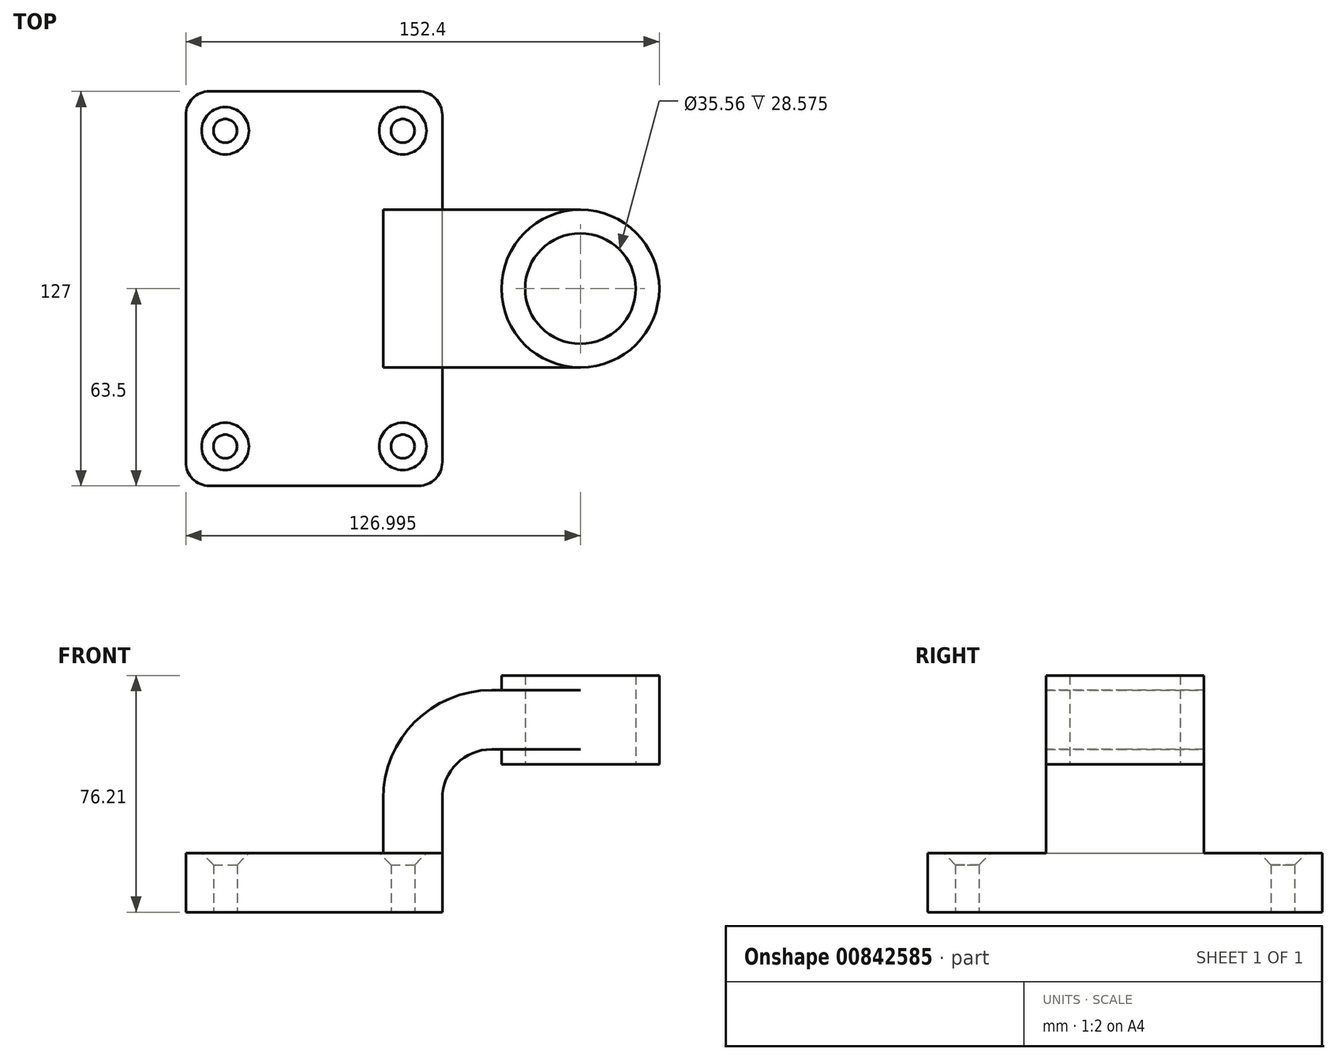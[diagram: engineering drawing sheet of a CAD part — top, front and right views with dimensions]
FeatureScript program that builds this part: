
annotation { "Feature Type Name" : "Feature", "Feature Type Description" : "" }
export const myFeature = defineFeature(function(context is Context, id is Id, definition is map)
    precondition{}
    {
        {
            var Q0;
            Q0=qCreatedBy(makeId("Front.planeOp"),FACE);
            var sketch = newSketch(context, id + "F0", { "sketchPlane" : qUnion([Q0])});
            skLineSegment(sketch, "E0.bottom", {"start": v(-41.28, 9.52) * mm, "end": v(41.27, 9.53) * mm});
            skLineSegment(sketch, "E0.top", {"start": v(-41.28, -9.53) * mm, "end": v(41.28, -9.53) * mm});
            skLineSegment(sketch, "E0.left", {"start": v(-41.28, 9.52) * mm, "end": v(-41.27, -9.53) * mm});
            skLineSegment(sketch, "E0.right", {"start": v(41.28, 9.53) * mm, "end": v(41.28, -9.52) * mm});
            skPoint(sketch, "E0.middle", {"position": v(0, 0) * mm});
            skLineSegment(sketch, "E1.bottom", {"start": v(111.13, 38.1) * mm, "end": v(60.33, 38.1) * mm});
            skLineSegment(sketch, "E1.top", {"start": v(111.13, 66.67) * mm, "end": v(60.33, 66.67) * mm});
            skLineSegment(sketch, "E1.left", {"start": v(111.13, 38.1) * mm, "end": v(111.13, 66.67) * mm});
            skLineSegment(sketch, "E1.right", {"start": v(60.33, 38.1) * mm, "end": v(60.33, 66.67) * mm});
            skPoint(sketch, "E1.middle", {"position": v(85.73, 52.39) * mm});
            skLineSegment(sketch, "E2", {"start": v(41.27, 9.53) * mm, "end": v(41.27, 27) * mm});
            skArc(sketch, "E3", {"start": v(41.27, 27) * mm, "mid": v(45.92, 38.23) * mm, "end": v(57.15, 42.88) * mm});
            skLineSegment(sketch, "E4", {"start": v(57.15, 42.88) * mm, "end": v(85.73, 42.88) * mm});
            skLineSegment(sketch, "E5.0", {"start": v(57.15, 61.93) * mm, "end": v(85.73, 61.93) * mm});
            skArc(sketch, "E5.1", {"start": v(22.22, 27) * mm, "mid": v(32.45, 51.7) * mm, "end": v(57.15, 61.93) * mm});
            skLineSegment(sketch, "E5.2", {"start": v(22.22, 9.53) * mm, "end": v(22.22, 27) * mm});
            skLineSegment(sketch, "E6", {"start": v(85.73, 38.1) * mm, "end": v(85.73, 66.67) * mm});
            skFitSpline(sketch, "E7", {"points": [v(-41.28, 9.53) * mm, v(57.15, 61.93) * mm], "startDerivative": vector(-0.26, 81.95) * mm, "endDerivative": vector(119.33, -1.8) * mm});
            skSolve(sketch);
        }
        {
            var Q0;
            Q0=makeQuery(id+"F0.imprint","IMPRINT",FACE,{"disambiguationData":[TD([[makeQuery(id+"F0.imprint","IMPRINT",EDGE,{"derivedFrom":sQuery(id+"F0.wireOp",EDGE,"E0.top")}),1.0]])]});
            extrude(context, id + "F1", {"entities" : qUnion([Q0]), "depth" : 127 * mm, "offsetDistance" : 25.4 * mm, "symmetric" : true});
        }
        {
            var Q0;
            {var subQ1=sQuery(id+"F0.wireOp",EDGE,"E2");Q0=makeQuery(id+"F0.imprint","IMPRINT",FACE,{"disambiguationData":[TD([[makeQuery(id+"F0.imprint","IMPRINT",EDGE,{"derivedFrom":subQ1}),1.0]])]});}
            var Q1;
            {var subQ0=sQuery(id+"F0.wireOp",EDGE,"E4");var subQ1=sQuery(id+"F0.wireOp",EDGE,"E1.right");var subQ2=makeQuery(id+"F0.imprint","INTERSECT",VERTEX,{"derivedFrom":[subQ1,subQ0]});Q1=makeQuery(id+"F0.imprint","IMPRINT",FACE,{"disambiguationData":[TD([[makeQuery(id+"F0.imprint","IMPRINT",EDGE,{"disambiguationData":[TD([[subQ2,-1.0]])],"derivedFrom":subQ1}),-1.0]])]});}
            extrude(context, id + "F2", {"entities" : qUnion([Q0, Q1]), "operationType" : NewBodyOperationType.ADD, "depth" : 50.8 * mm, "offsetDistance" : 25.4 * mm, "symmetric" : true});
        }
        {
            var Q0;
            Q0=makeQuery(id+"F0.imprint","IMPRINT",FACE,{"disambiguationData":[TD([[makeQuery(id+"F0.imprint","IMPRINT",EDGE,{"derivedFrom":sQuery(id+"F0.wireOp",EDGE,"E5.1")}),1.0]])]});
            extrude(context, id + "F3", {"entities" : qUnion([Q0]), "operationType" : NewBodyOperationType.ADD, "depth" : 15.88 * mm, "offsetDistance" : 25.4 * mm, "symmetric" : true});
        }
        {
            var Q0;
            {var subQ4=sQuery(id+"F0.wireOp",EDGE,"E1.left");Q0=makeQuery(id+"F0.imprint","IMPRINT",FACE,{"disambiguationData":[TD([[makeQuery(id+"F0.imprint","IMPRINT",EDGE,{"derivedFrom":subQ4}),1.0]])]});}
            var Q1;
            Q1=sQuery(id+"F0.wireOp",EDGE,"E6");
            revolve(context, id + "F4", {"operationType" : NewBodyOperationType.ADD, "surfaceOperationType" : NewSurfaceOperationType.NEW, "entities" : qUnion([Q0]), "axis" : qUnion([Q1]), "revolveType" : RevolveType.FULL});
        }
        {
            var Q0;
            Q0=makeQuery(id+"F1.opExtrude","CAP_EDGE",EDGE,{"disambiguationData":[OSD([sQuery(id+"F0.wireOp",EDGE,"E0.left")])],"isStart":false});
            var Q1;
            Q1=makeQuery(id+"F1.opExtrude","CAP_EDGE",EDGE,{"disambiguationData":[OSD([sQuery(id+"F0.wireOp",EDGE,"E0.right")])],"isStart":false});
            var Q2;
            Q2=makeQuery(id+"F1.opExtrude","CAP_EDGE",EDGE,{"disambiguationData":[OSD([sQuery(id+"F0.wireOp",EDGE,"E0.left")])],"isStart":true});
            var Q3;
            Q3=makeQuery(id+"F1.opExtrude","CAP_EDGE",EDGE,{"disambiguationData":[OSD([sQuery(id+"F0.wireOp",EDGE,"E0.right")])],"isStart":true});
            fillet(context, id + "F5", {"entities" : qUnion([Q0, Q1, Q2, Q3]), "radius" : 7.62 * mm, "tangentPropagation" : true, "allowEdgeOverflow" : false});
        }
        {
            var Q0;
            {var subQ3=sQuery(id+"F0.wireOp",EDGE,"E0.bottom");var subQ4=sQuery(id+"F0.wireOp",EDGE,"E0.right");var subQ5=sQuery(id+"F0.wireOp",EDGE,"E0.left");Q0=makeQuery(id+"F3.boolean.opBoolean","SPLIT",FACE,{"disambiguationData":[TD([makeQuery(id+"F1.opExtrude","CAP_FACE",FACE,{"disambiguationData":[OSD([subQ3,sQuery(id+"F0.wireOp",EDGE,"E0.top"),subQ5,subQ4])],"isStart":true})])],"derivedFrom":makeQuery(id+"F1.opExtrude","SWEPT_FACE",FACE,{"disambiguationData":[OSD([subQ3])]})});}
            var sketch = newSketch(context, id + "F6", { "sketchPlane" : qUnion([Q0])});
            skLineSegment(sketch, "E8", {"start": v(-28.58, 63.5) * mm, "end": v(-28.58, -63.43) * mm});
            skLineSegment(sketch, "E9", {"start": v(28.57, 63.5) * mm, "end": v(28.58, -64.39) * mm});
            skLineSegment(sketch, "E10", {"start": v(-40.69, -50.8) * mm, "end": v(41.81, -50.8) * mm});
            skLineSegment(sketch, "E11", {"start": v(-41.28, 50.8) * mm, "end": v(41.27, 50.8) * mm});
            skPoint(sketch, "E12", {"position": v(-28.58, 50.8) * mm});
            skPoint(sketch, "E13", {"position": v(28.57, 50.8) * mm});
            skPoint(sketch, "E14", {"position": v(28.58, -50.8) * mm});
            skPoint(sketch, "E15", {"position": v(-28.58, -50.8) * mm});
            skSolve(sketch);
        }
        {
            var Q0;
            Q0=sQuery(id+"F6.wireOp",VERTEX,"E12");
            var Q1;
            Q1=makeQuery(id+"F1.opExtrude","SWEPT_BODY",BODY,{"disambiguationData":[OSD([sQuery(id+"F0.wireOp",EDGE,"E0.bottom"),sQuery(id+"F0.wireOp",EDGE,"E0.top"),sQuery(id+"F0.wireOp",EDGE,"E0.left"),sQuery(id+"F0.wireOp",EDGE,"E0.right")])]});
            hole(context, id + "F7", {"style" : HoleStyle.C_SINK, "endStyle" : HoleEndStyle.THROUGH, "holeDiameter" : 7.62 * mm, "cSinkDiameter" : 15.24 * mm, "cSinkAngle" : 90 * degree, "majorDiameter" : 6.35 * mm, "isTappedThrough" : true, "tappedDepth" : 12.7 * mm, "tapClearance" : 3, "locations" : qUnion([Q0]), "scope" : qUnion([Q1]), "startStyle" : HoleStartStyle.SKETCH});
        }
        {
            var Q0;
            Q0=sQuery(id+"F6.wireOp",VERTEX,"E15");
            var Q1;
            Q1=sQuery(id+"F6.wireOp",VERTEX,"E14");
            var Q2;
            Q2=sQuery(id+"F6.wireOp",VERTEX,"E13");
            var Q3;
            Q3=makeQuery(id+"F1.opExtrude","SWEPT_BODY",BODY,{"disambiguationData":[OSD([sQuery(id+"F0.wireOp",EDGE,"E0.bottom"),sQuery(id+"F0.wireOp",EDGE,"E0.top"),sQuery(id+"F0.wireOp",EDGE,"E0.left"),sQuery(id+"F0.wireOp",EDGE,"E0.right")])]});
            hole(context, id + "F8", {"style" : HoleStyle.C_SINK, "endStyle" : HoleEndStyle.THROUGH, "holeDiameter" : 7.62 * mm, "cSinkDiameter" : 15.24 * mm, "cSinkAngle" : 90 * degree, "majorDiameter" : 6.35 * mm, "isTappedThrough" : true, "tappedDepth" : 12.7 * mm, "tapClearance" : 3, "locations" : qUnion([Q0, Q1, Q2]), "scope" : qUnion([Q3]), "startStyle" : HoleStartStyle.SKETCH});
        }
        {
            var Q0;
            Q0=makeQuery(id+"F4.opRevolve","SWEPT_FACE",FACE,{"disambiguationData":[OSD([sQuery(id+"F0.wireOp",EDGE,"E1.top")])]});
            var sketch = newSketch(context, id + "F9", { "sketchPlane" : qUnion([Q0])});
            skPoint(sketch, "E16", {"position": v(85.72, 0) * mm});
            skSolve(sketch);
        }
        {
            var Q0;
            Q0=sQuery(id+"F9.wireOp",VERTEX,"E16");
            var Q1;
            Q1=makeQuery(id+"F1.opExtrude","SWEPT_BODY",BODY,{"disambiguationData":[OSD([sQuery(id+"F0.wireOp",EDGE,"E0.bottom"),sQuery(id+"F0.wireOp",EDGE,"E0.top"),sQuery(id+"F0.wireOp",EDGE,"E0.left"),sQuery(id+"F0.wireOp",EDGE,"E0.right")])]});
            hole(context, id + "F10", {"style" : HoleStyle.SIMPLE, "endStyle" : HoleEndStyle.THROUGH, "holeDiameter" : 35.56 * mm, "majorDiameter" : 6.35 * mm, "isTappedThrough" : true, "tappedDepth" : 12.7 * mm, "tapClearance" : 3, "locations" : qUnion([Q0]), "scope" : qUnion([Q1]), "startStyle" : HoleStartStyle.SKETCH});
        }
    });
